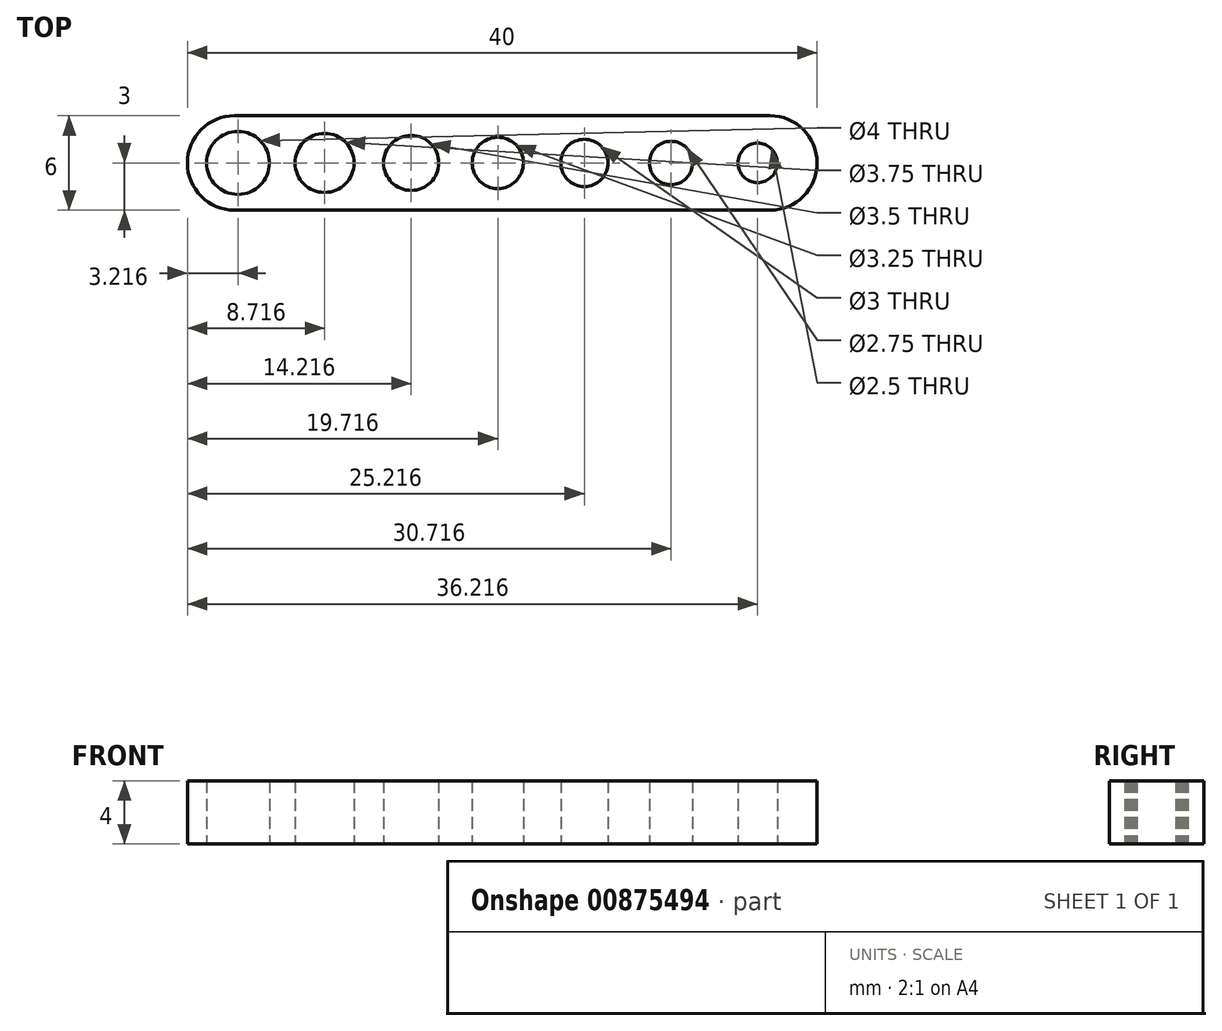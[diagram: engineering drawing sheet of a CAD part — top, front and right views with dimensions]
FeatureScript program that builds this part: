
annotation { "Feature Type Name" : "Feature", "Feature Type Description" : "" }
export const myFeature = defineFeature(function(context is Context, id is Id, definition is map)
    precondition{}
    {
        {
            var Q0;
            Q0=qCreatedBy(makeId("Top.planeOp"),FACE);
            var sketch = newSketch(context, id + "F0", { "sketchPlane" : qUnion([Q0])});
            skLineSegment(sketch, "E0.bottom", {"start": v(0, 0) * mm, "end": v(-40, 0) * mm});
            skLineSegment(sketch, "E0.top", {"start": v(0, 6) * mm, "end": v(-40, 6) * mm});
            skLineSegment(sketch, "E0.left", {"start": v(0, 0) * mm, "end": v(0, 6) * mm});
            skLineSegment(sketch, "E0.right", {"start": v(-40, 0) * mm, "end": v(-40, 6) * mm});
            skCircle(sketch, "E1", {"center": v(-36.78, 3) * mm, "radius": 2 * mm});
            skCircle(sketch, "E2.1.0.0", {"center": v(-31.28, 3) * mm, "radius": 1.88 * mm});
            skCircle(sketch, "E2.2.0.0", {"center": v(-25.78, 3) * mm, "radius": 1.75 * mm});
            skCircle(sketch, "E2.3.0.0", {"center": v(-20.28, 3) * mm, "radius": 1.63 * mm});
            skCircle(sketch, "E2.4.0.0", {"center": v(-14.78, 3) * mm, "radius": 1.5 * mm});
            skCircle(sketch, "E2.5.0.0", {"center": v(-9.28, 3) * mm, "radius": 1.38 * mm});
            skLineSegment(sketch, "E2.direction1", {"start": v(-36.78, 3) * mm, "end": v(-31.28, 3) * mm, "construction": true});
            skCircle(sketch, "E3.0.6.0", {"center": v(-3.78, 3) * mm, "radius": 1.25 * mm});
            skSolve(sketch);
        }
        {
            var Q0;
            Q0=makeQuery(id+"F0.imprint","IMPRINT",FACE,{"disambiguationData":[TD([[makeQuery(id+"F0.imprint","IMPRINT",EDGE,{"derivedFrom":sQuery(id+"F0.wireOp",EDGE,"E0.bottom")}),-1.0]])]});
            extrude(context, id + "F1", {"entities" : qUnion([Q0]), "depth" : 4 * mm, "offsetDistance" : 25 * mm});
        }
        {
            var Q0;
            Q0=makeQuery(id+"F1.opExtrude","SWEPT_EDGE",EDGE,{"disambiguationData":[OSD([sQuery(id+"F0.wireOp",EDGE,"E0.bottom"),sQuery(id+"F0.wireOp",EDGE,"E0.left")])]});
            var Q1;
            Q1=makeQuery(id+"F1.opExtrude","SWEPT_EDGE",EDGE,{"disambiguationData":[OSD([sQuery(id+"F0.wireOp",EDGE,"E0.top"),sQuery(id+"F0.wireOp",EDGE,"E0.left")])]});
            var Q2;
            Q2=makeQuery(id+"F1.opExtrude","SWEPT_EDGE",EDGE,{"disambiguationData":[OSD([sQuery(id+"F0.wireOp",EDGE,"E0.bottom"),sQuery(id+"F0.wireOp",EDGE,"E0.right")])]});
            var Q3;
            Q3=makeQuery(id+"F1.opExtrude","SWEPT_EDGE",EDGE,{"disambiguationData":[OSD([sQuery(id+"F0.wireOp",EDGE,"E0.top"),sQuery(id+"F0.wireOp",EDGE,"E0.right")])]});
            fillet(context, id + "F2", {"entities" : qUnion([Q0, Q1, Q2, Q3]), "radius" : 3 * mm, "tangentPropagation" : true, "allowEdgeOverflow" : false});
        }
    });
